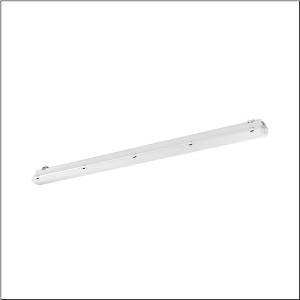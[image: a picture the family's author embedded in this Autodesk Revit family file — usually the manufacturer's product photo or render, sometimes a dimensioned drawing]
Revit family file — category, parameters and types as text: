
# Revit family: monsun_r__11xtreme_mo_51fe10dp440j_05e8
name_source: partatom
category: Lighting Fixtures
units: mm (PartAtom-declared; Revit-internal decimal feet)

## family parameters
Cut with Voids When Loaded = No
Host = Face
Light Source = No
Part Type = Normal
Room Calculation Point = No
Round Connector Dimension = Use Diameter
Shared = No

## types (1)
- --- (1 x LED, 4200 lm, 24.2 W, 4000K)
    Apparent Load = 24 VA
    CIE Flux Codes = 47 77 93 94 100
    Color Rendering = 80
    Color Temperature = 4000K
    Default Elevation = 1800 mm
    Description = Monsun® 11Xtreme MO, damp-proof luminaire, chain hanger, primary optical cover: enclosure, of PMMA, light emission: direct distribution, primary light characteristic: symmetric, installation type: suspended mounting, surface-mounted, horizontal mounting, vertical mounting, LED, rated luminous flux: 4.200lm, luminous efficacy: 174lm/W, light colour: 840, colour temperature: 4000K, control gear: ECG DALI, with terminal, 5-pole, max. 2.5mm², mains connection: 220..240V, AC, 50/60Hz, rated input power: 24W, luminaire housing, of glass-fibre reinforced polyester, uncoated, bright grey, incl. chain hanger, length: 1.590mm, width: 90mm, height: 88mm, clip for enclosure, of stainless steel (V2A), ceiling mounting element, of stainless steel (V2A), chain hanger, of stainless steel (V2A), protection rating (complete): IP66, insulation class (complete): insulation class I (protective earthing), certification: CE, ENEC, VDE, UKCA, protection symbol: D, impact resistance: IK04, permissible operating ambient temperature: -25..+50°C, standard: EN 60598-2-1, EN 50419, corresponds to IFS (International Featured Standards) requirements for safety and quality in the food industry, for indoor or canopied outdoor use, no direct snow, no direct sun, no direct rain, contact your sales advisor before using the luminaires in applications with unclear chemical exposure, large temperature fluctuations or condensation-forming humidity, LABS conformity tested according to VDMA 24364:2018-05, packaging unit: 1 piece
    Height = 88 mm
    Lamp = 1 x LED
    Lamp Light Flux = 4200 lm
    Lamp Power = 24.2 W
    Lamp count = 1
    Length = 1590 mm
    Luminous efficacy = 174 lm/W
    Manufacturer = Siteco
    ModVariant = No
    Model = 51FE10DP440J
    Mounting Place = Ceiling
    Mounting Type = Surface mounted
    Number of Poles = 1
    OnlyDefault = Yes
    Power Factor = 1
    Product Name = Monsun® 11Xtreme MO
    Product group = damp-proof luminaire
    ProductGroupID = 301
    Protection Class = Protection class I
    Protection Degree = IP 66
    RLX_Detail_Level = 1
    RLX_Emergency_Light_Flux = 0 lm
    RLX_Emergency_Type = 0
    RLX_Emergency_Type_DB = No
    RlxData = <blob elided: 87345 chars, md5=c702f688>
    Socket = socket
    Standby Power = 0 W
    System Light Flux = 4200 lm
    System Power = 24 W
    Type Comments = factory setting: luminous flux: 100 % | dim-lin: 254 | 159 mA
    Type Image = l_1006851.jpg
    URL = http://relux.com
    VarID = @adj_151123
    Voltage = 0 V
    Weight = 0.00 kg
    Width = 90 mm

## geometry (parser evidence)
native form markers: Blend x4, Sweep x13
no freeform markers — native parametric forms only
